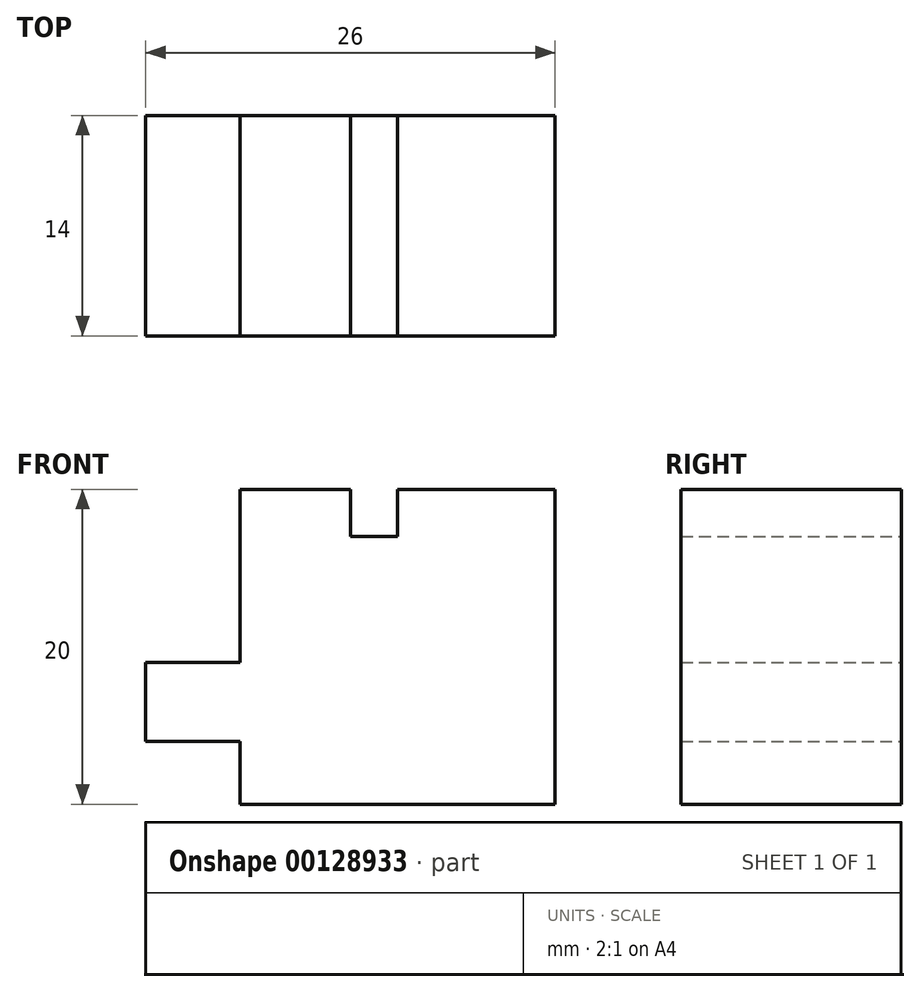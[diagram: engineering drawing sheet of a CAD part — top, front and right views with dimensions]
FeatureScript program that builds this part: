
annotation { "Feature Type Name" : "Feature", "Feature Type Description" : "" }
export const myFeature = defineFeature(function(context is Context, id is Id, definition is map)
    precondition{}
    {
        {
            var Q0;
            Q0=qCreatedBy(makeId("Front.planeOp"),FACE);
            var sketch = newSketch(context, id + "F0", { "sketchPlane" : qUnion([Q0])});
            skLineSegment(sketch, "E0", {"start": v(9.06, 0) * mm, "end": v(9.06, 20) * mm});
            skLineSegment(sketch, "E1", {"start": v(-10.94, 0) * mm, "end": v(-10.94, 4) * mm});
            skLineSegment(sketch, "E2", {"start": v(-10.94, 20) * mm, "end": v(-10.94, 9) * mm});
            skLineSegment(sketch, "E3", {"start": v(9.06, 20) * mm, "end": v(-0.94, 20) * mm});
            skLineSegment(sketch, "E4", {"start": v(-0.94, 20) * mm, "end": v(-0.94, 17) * mm});
            skLineSegment(sketch, "E5", {"start": v(-0.94, 17) * mm, "end": v(-3.94, 17) * mm});
            skLineSegment(sketch, "E6", {"start": v(-3.94, 17) * mm, "end": v(-3.94, 20) * mm});
            skLineSegment(sketch, "E7", {"start": v(-10.94, 20) * mm, "end": v(-3.94, 20) * mm});
            skLineSegment(sketch, "E8", {"start": v(-10.94, 4) * mm, "end": v(-16.94, 4) * mm});
            skLineSegment(sketch, "E9", {"start": v(-16.94, 4) * mm, "end": v(-16.94, 9) * mm});
            skLineSegment(sketch, "E10", {"start": v(-16.94, 9) * mm, "end": v(-10.94, 9) * mm});
            skLineSegment(sketch, "E11", {"start": v(-10.94, 0) * mm, "end": v(9.06, 0) * mm});
            skSolve(sketch);
        }
        {
            var Q0;
            Q0 = qSketchRegion(id + "F0", true);
            extrude(context, id + "F1", {"entities" : qUnion([Q0]), "depth" : 14 * mm});
        }
    });
